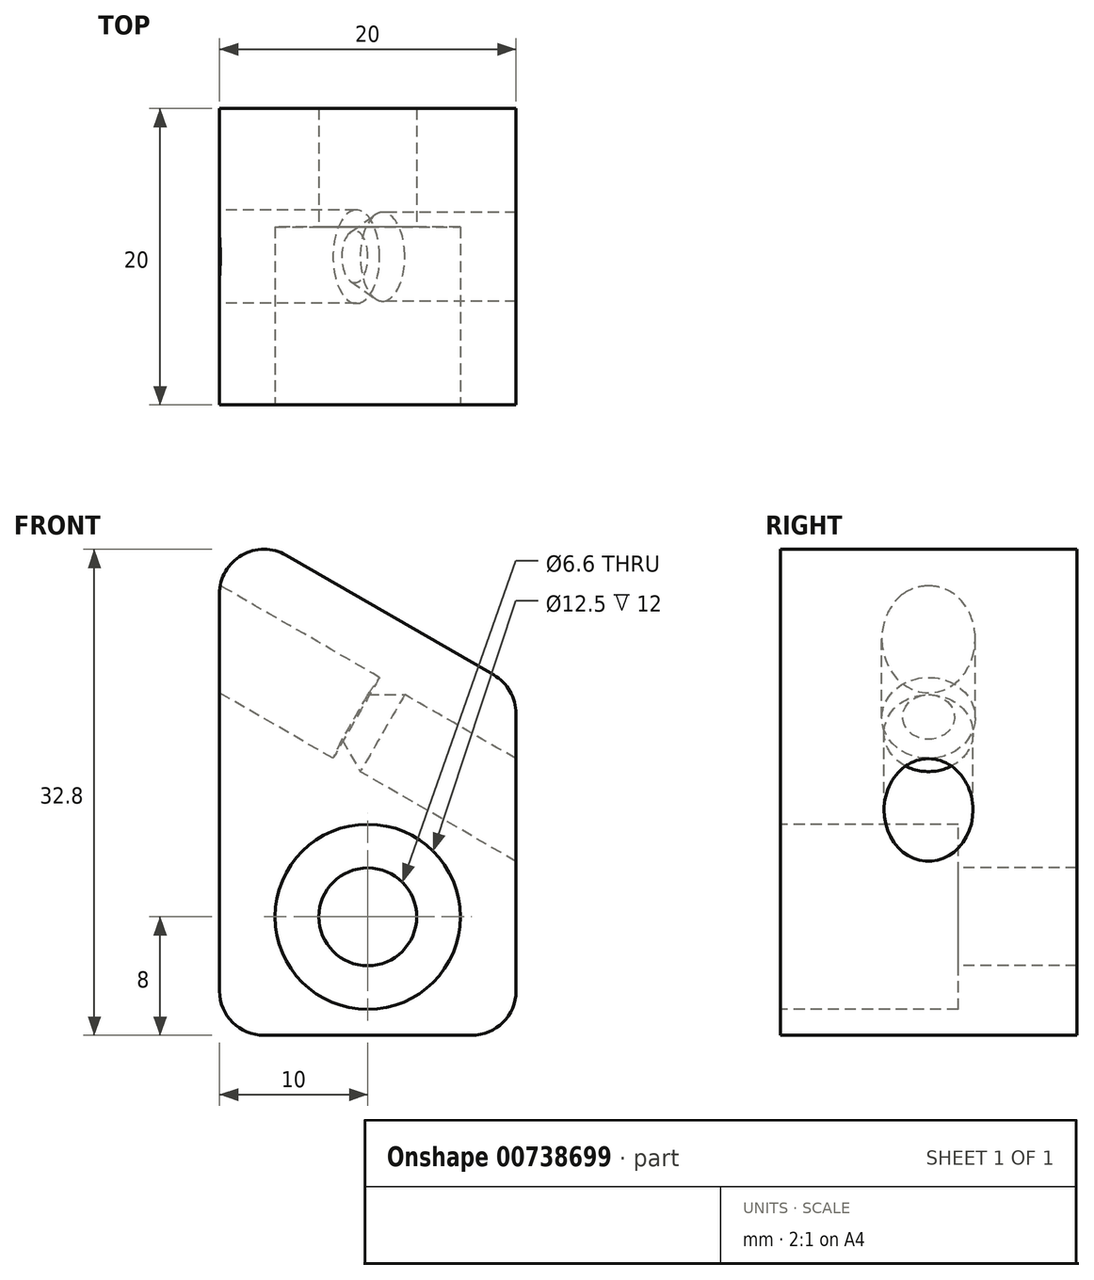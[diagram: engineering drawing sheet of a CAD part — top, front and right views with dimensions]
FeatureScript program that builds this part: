
annotation { "Feature Type Name" : "Feature", "Feature Type Description" : "" }
export const myFeature = defineFeature(function(context is Context, id is Id, definition is map)
    precondition{}
    {
        {
            var Q0;
            Q0=qCreatedBy(makeId("Front.planeOp"),FACE);
            var sketch = newSketch(context, id + "F0", { "sketchPlane" : qUnion([Q0])});
            skLineSegment(sketch, "E0.top", {"start": v(10, -20) * mm, "end": v(-10, -20) * mm});
            skPoint(sketch, "E0.middle", {"position": v(0, 0) * mm});
            skLineSegment(sketch, "E1", {"start": v(-10, 15) * mm, "end": v(10, 3.45) * mm});
            skLineSegment(sketch, "E2", {"start": v(-10, 15) * mm, "end": v(-10, -20) * mm});
            skLineSegment(sketch, "E3", {"start": v(10, -20) * mm, "end": v(10, 3.45) * mm});
            skSolve(sketch);
        }
        {
            var Q0;
            Q0 = qSketchRegion(id + "F0", true);
            extrude(context, id + "F1", {"entities" : qUnion([Q0]), "depth" : 20 * mm, "offsetDistance" : 25 * mm});
        }
        {
            var Q0;
            Q0=makeQuery(id+"F1.opExtrude","CAP_FACE",FACE,{"disambiguationData":[OSD([sQuery(id+"F0.wireOp",EDGE,"E0.top"),sQuery(id+"F0.wireOp",EDGE,"E1"),sQuery(id+"F0.wireOp",EDGE,"E2"),sQuery(id+"F0.wireOp",EDGE,"E3")])],"isStart":false});
            cPlane(context, id + "F2", {"entities" : qUnion([Q0]), "cplaneType" : CPlaneType.OFFSET, "offset" : 10 * mm, "oppositeDirection" : true, "width" : 150 * mm, "height" : 150 * mm});
        }
        {
            var Q0;
            Q0=qCreatedBy(id+"F2.planeOp",FACE);
            var sketch = newSketch(context, id + "F3", { "sketchPlane" : qUnion([Q0])});
            skPoint(sketch, "E4.middle", {"position": v(0, 3) * mm});
            skLineSegment(sketch, "E5", {"start": v(-10.4, 6.98) * mm, "end": v(-10.4, 10.62) * mm});
            skLineSegment(sketch, "E6", {"start": v(0, 3) * mm, "end": v(0.8, 4.15) * mm});
            skLineSegment(sketch, "E7", {"start": v(-10.4, 10.62) * mm, "end": v(0.8, 4.15) * mm});
            skLineSegment(sketch, "E8", {"start": v(0, 3) * mm, "end": v(2.5, 3) * mm});
            skLineSegment(sketch, "E9", {"start": v(13.37, -3.27) * mm, "end": v(2.5, 3) * mm});
            skLineSegment(sketch, "E10", {"start": v(13.37, -3.27) * mm, "end": v(13.37, -6.74) * mm});
            skLineSegment(sketch, "E11", {"start": v(13.37, -6.74) * mm, "end": v(-10.4, 6.98) * mm});
            skSolve(sketch);
        }
        {
            var Q0;
            Q0=makeQuery(id+"F1.opExtrude","CAP_FACE",FACE,{"disambiguationData":[OSD([sQuery(id+"F0.wireOp",EDGE,"E0.bottom"),sQuery(id+"F0.wireOp",EDGE,"E0.top"),sQuery(id+"F0.wireOp",EDGE,"E0.left"),sQuery(id+"F0.wireOp",EDGE,"E0.right")])],"isStart":false});
            var sketch = newSketch(context, id + "F4", { "sketchPlane" : qUnion([Q0])});
            skPoint(sketch, "E12", {"position": v(0, -12) * mm});
            skSolve(sketch);
        }
        {
            var Q0;
            Q0=sQuery(id+"F4.wireOp",VERTEX,"E12");
            var Q1;
            Q1=makeQuery(id+"F1.opExtrude","SWEPT_BODY",BODY,{"disambiguationData":[OSD([sQuery(id+"F0.wireOp",EDGE,"E0.bottom"),sQuery(id+"F0.wireOp",EDGE,"E0.top"),sQuery(id+"F0.wireOp",EDGE,"E0.left"),sQuery(id+"F0.wireOp",EDGE,"E0.right")])]});
            hole(context, id + "F5", {"style" : HoleStyle.C_BORE, "endStyle" : HoleEndStyle.THROUGH, "holeDiameter" : 6.6 * mm, "cBoreDiameter" : 12.5 * mm, "cBoreDepth" : 12 * mm, "majorDiameter" : 5 * mm, "isTappedThrough" : true, "tappedDepth" : 12 * mm, "tapClearance" : 3, "locations" : qUnion([Q0]), "scope" : qUnion([Q1])});
        }
        {
            var Q0;
            Q0=makeQuery(id+"F3.imprint","IMPRINT",FACE,{"disambiguationData":[TD([[makeQuery(id+"F3.imprint","IMPRINT",EDGE,{"derivedFrom":sQuery(id+"F3.wireOp",EDGE,"E5")}),-1.0]])]});
            var Q1;
            Q1=sQuery(id+"F3.wireOp",EDGE,"E11");
            revolve(context, id + "F6", {"operationType" : NewBodyOperationType.REMOVE, "surfaceOperationType" : NewSurfaceOperationType.NEW, "entities" : qUnion([Q0]), "axis" : qUnion([Q1]), "revolveType" : RevolveType.FULL, "oppositeDirection" : true});
        }
        {
            var Q0;
            Q0=makeQuery(id+"F1.opExtrude","SWEPT_EDGE",EDGE,{"disambiguationData":[OSD([sQuery(id+"F0.wireOp",EDGE,"E1"),sQuery(id+"F0.wireOp",EDGE,"E2")])]});
            var Q1;
            Q1=makeQuery(id+"F1.opExtrude","SWEPT_EDGE",EDGE,{"disambiguationData":[OSD([sQuery(id+"F0.wireOp",EDGE,"E1"),sQuery(id+"F0.wireOp",EDGE,"E3")])]});
            var Q2;
            Q2=makeQuery(id+"F1.opExtrude","SWEPT_EDGE",EDGE,{"disambiguationData":[OSD([sQuery(id+"F0.wireOp",EDGE,"E0.top"),sQuery(id+"F0.wireOp",EDGE,"E3")])]});
            var Q3;
            Q3=makeQuery(id+"F1.opExtrude","SWEPT_EDGE",EDGE,{"disambiguationData":[OSD([sQuery(id+"F0.wireOp",EDGE,"E0.top"),sQuery(id+"F0.wireOp",EDGE,"E2")])]});
            fillet(context, id + "F7", {"entities" : qUnion([Q0, Q1, Q2, Q3]), "radius" : 3 * mm, "tangentPropagation" : true, "allowEdgeOverflow" : false});
        }
    });
